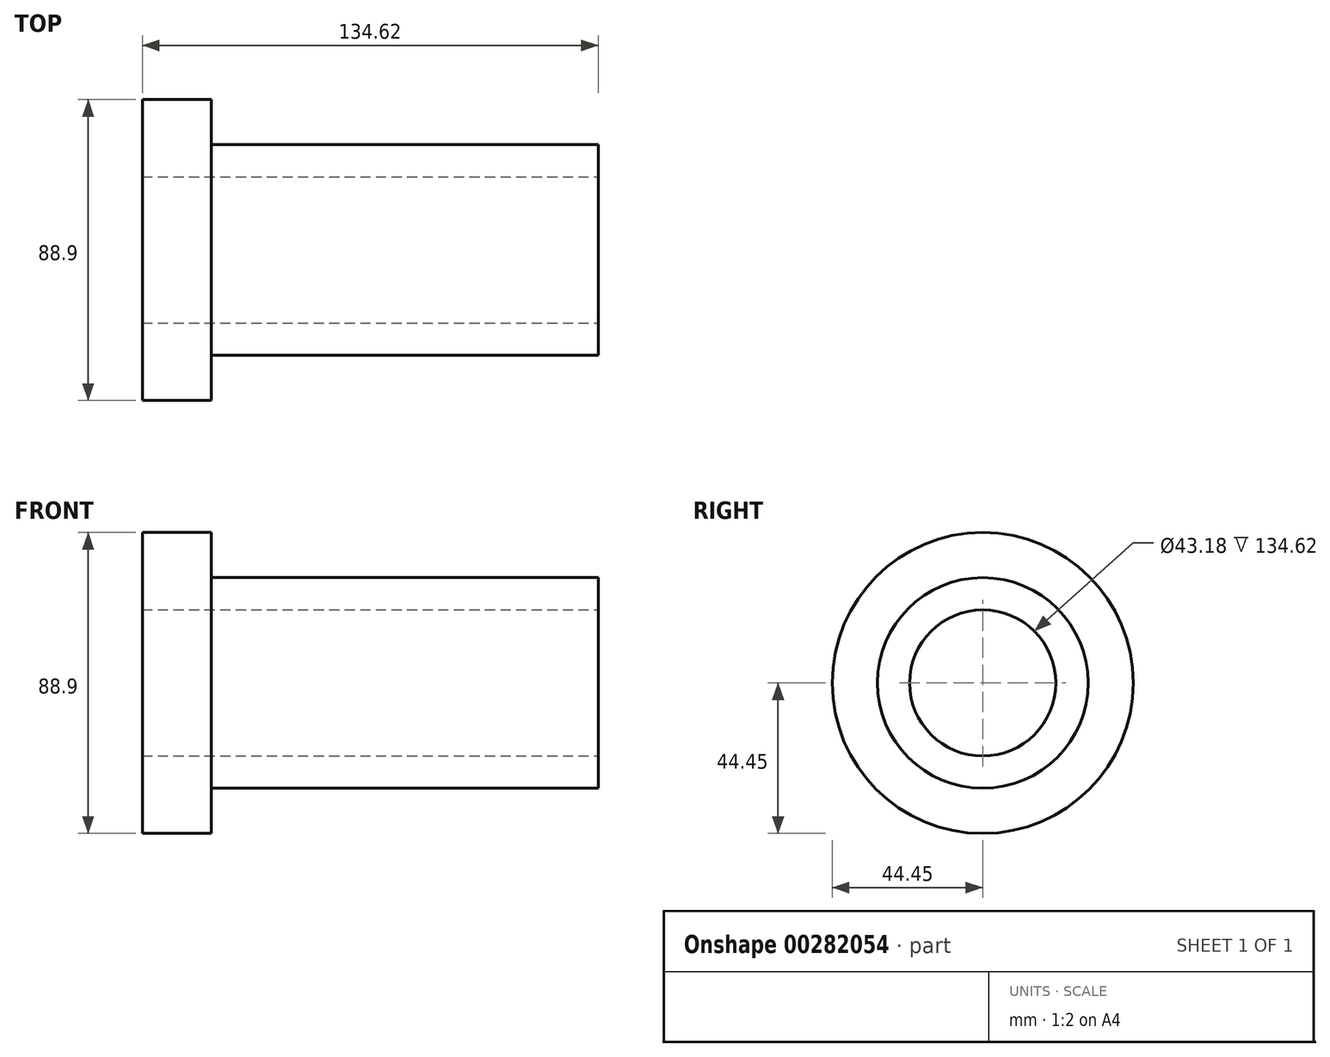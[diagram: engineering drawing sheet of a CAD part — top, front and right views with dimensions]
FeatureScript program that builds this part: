
annotation { "Feature Type Name" : "Feature", "Feature Type Description" : "" }
export const myFeature = defineFeature(function(context is Context, id is Id, definition is map)
    precondition{}
    {
        {
            var Q0;
            Q0=qCreatedBy(makeId("Front.planeOp"),FACE);
            var sketch = newSketch(context, id + "F0", { "sketchPlane" : qUnion([Q0])});
            skLineSegment(sketch, "E0", {"start": v(0, 21.59) * mm, "end": v(0, 31.12) * mm});
            skLineSegment(sketch, "E1", {"start": v(0, 31.12) * mm, "end": v(-114.3, 31.11) * mm});
            skLineSegment(sketch, "E2", {"start": v(-114.3, 31.11) * mm, "end": v(-114.3, 44.45) * mm});
            skLineSegment(sketch, "E3", {"start": v(-114.3, 44.45) * mm, "end": v(-134.62, 44.45) * mm});
            skLineSegment(sketch, "E4", {"start": v(-134.62, 44.45) * mm, "end": v(-134.62, 21.59) * mm});
            skLineSegment(sketch, "E5", {"start": v(-134.62, 21.59) * mm, "end": v(0, 21.59) * mm});
            skLineSegment(sketch, "E6", {"start": v(15.78, 0) * mm, "end": v(-80.71, 0) * mm, "construction": true});
            skSolve(sketch);
        }
        {
            var Q0;
            Q0=makeQuery(id+"F0.imprint","IMPRINT",FACE,{"disambiguationData":[TD([[makeQuery(id+"F0.imprint","IMPRINT",EDGE,{"derivedFrom":sQuery(id+"F0.wireOp",EDGE,"E0")}),1.0]])]});
            var Q1;
            Q1=sQuery(id+"F0.wireOp",EDGE,"E6");
            revolve(context, id + "F1", {"entities" : qUnion([Q0]), "axis" : qUnion([Q1]), "revolveType" : RevolveType.FULL});
        }
    });
